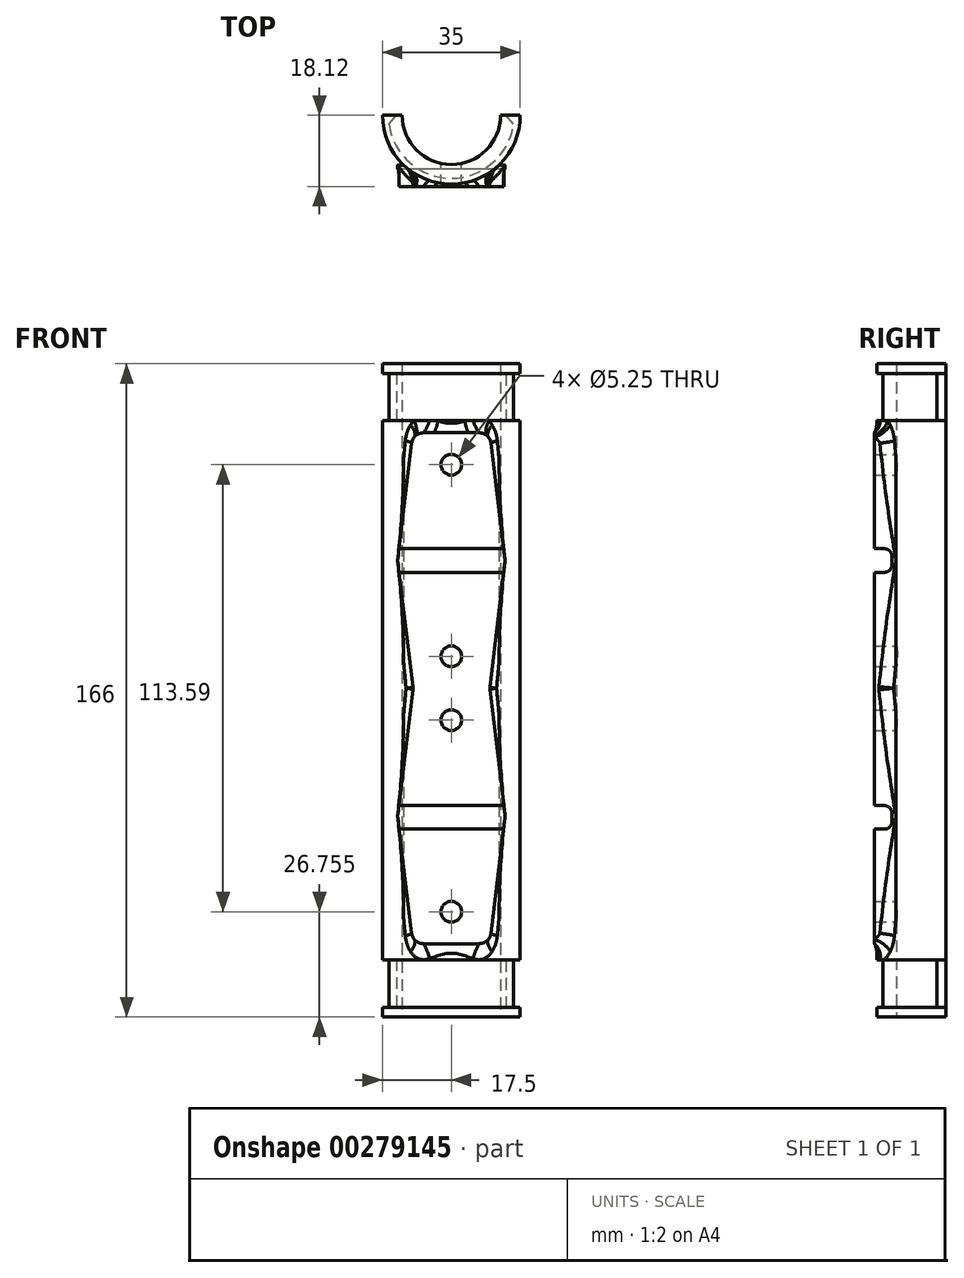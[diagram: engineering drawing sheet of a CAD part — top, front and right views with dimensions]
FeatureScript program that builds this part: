
annotation { "Feature Type Name" : "Feature", "Feature Type Description" : "" }
export const myFeature = defineFeature(function(context is Context, id is Id, definition is map)
    precondition{}
    {
        {
            var Q0;
            Q0=qCreatedBy(makeId("Front.planeOp"),FACE);
            var sketch = newSketch(context, id + "F0", { "sketchPlane" : qUnion([Q0])});
            skLineSegment(sketch, "E0", {"start": v(-13.65, 0) * mm, "end": v(-9.75, 32.45) * mm});
            skLineSegment(sketch, "E1", {"start": v(-9.75, 32.45) * mm, "end": v(9.75, 32.45) * mm});
            skLineSegment(sketch, "E2", {"start": v(9.75, 32.45) * mm, "end": v(13.65, 0) * mm});
            skLineSegment(sketch, "E3.MirrorCS", {"start": v(-13.65, 0) * mm, "end": v(-9.75, -32.45) * mm});
            skLineSegment(sketch, "E4.MirrorCS", {"start": v(9.75, -32.45) * mm, "end": v(13.65, 0) * mm});
            skLineSegment(sketch, "E5.MirrorCS", {"start": v(-9.75, -32.45) * mm, "end": v(9.75, -32.45) * mm});
            skCircle(sketch, "E6", {"center": v(0, 24.35) * mm, "radius": 2.63 * mm});
            skCircle(sketch, "E7.MirrorC", {"center": v(0, -24.35) * mm, "radius": 2.63 * mm});
            skLineSegment(sketch, "E8", {"start": v(-60.1, -32.45) * mm, "end": v(71.13, -32.45) * mm});
            skLineSegment(sketch, "E9.MirrorCS", {"start": v(-13.65, -64.9) * mm, "end": v(-9.75, -32.45) * mm});
            skLineSegment(sketch, "E10.MirrorCS", {"start": v(9.75, -32.45) * mm, "end": v(13.65, -64.9) * mm});
            skLineSegment(sketch, "E11.MirrorCS", {"start": v(9.75, -97.35) * mm, "end": v(13.65, -64.9) * mm});
            skCircle(sketch, "E12.MirrorC", {"center": v(0, -89.25) * mm, "radius": 2.63 * mm});
            skCircle(sketch, "E13.MirrorC", {"center": v(0, -40.56) * mm, "radius": 2.63 * mm});
            skLineSegment(sketch, "E14.MirrorCS", {"start": v(-13.65, -64.9) * mm, "end": v(-9.75, -97.35) * mm});
            skLineSegment(sketch, "E15.MirrorCS", {"start": v(-9.75, -97.35) * mm, "end": v(9.75, -97.35) * mm});
            skSolve(sketch);
        }
        {
            var Q0;
            Q0=makeQuery(id+"F0.imprint","IMPRINT",FACE,{"disambiguationData":[TD([[makeQuery(id+"F0.imprint","IMPRINT",EDGE,{"derivedFrom":sQuery(id+"F0.wireOp",EDGE,"E0")}),-1.0]])]});
            extrude(context, id + "F1", {"entities" : qUnion([Q0]), "depth" : 5.5 * mm});
        }
        {
            var Q0;
            Q0=qCreatedBy(makeId("Top.planeOp"),FACE);
            var sketch = newSketch(context, id + "F2", { "sketchPlane" : qUnion([Q0])});
            skCircle(sketch, "E16", {"center": v(0, 12.62) * mm, "radius": 12.5 * mm});
            skCircle(sketch, "E17", {"center": v(0, 12.62) * mm, "radius": 17.5 * mm});
            skLineSegment(sketch, "E18", {"start": v(-24.24, 12.62) * mm, "end": v(25.02, 12.62) * mm});
            skLineSegment(sketch, "E19", {"start": v(25.02, 12.62) * mm, "end": v(2.17, 34.86) * mm});
            skLineSegment(sketch, "E20", {"start": v(2.17, 34.86) * mm, "end": v(-24.24, 12.62) * mm});
            skSolve(sketch);
        }
        {
            var Q0;
            {var subQ0=sQuery(id+"F2.wireOp",EDGE,"E18");var subQ1=sQuery(id+"F2.wireOp",EDGE,"E16");var subQ2=makeQuery(id+"F2.imprint","INTERSECT",VERTEX,{"disambiguationData":[OD(0.0)],"derivedFrom":[subQ1,subQ0]});Q0=makeQuery(id+"F2.imprint","IMPRINT",FACE,{"disambiguationData":[TD([[makeQuery(id+"F2.imprint","IMPRINT",EDGE,{"disambiguationData":[TD([[subQ2,-1.0]])],"derivedFrom":subQ1}),-1.0]])]});}
            var Q1;
            Q1=makeQuery(id+"F1.opExtrude","SWEPT_FACE",FACE,{"disambiguationData":[OSD([sQuery(id+"F0.wireOp",EDGE,"E1")])]});
            extrude(context, id + "F3", {"entities" : qUnion([Q0]), "operationType" : NewBodyOperationType.ADD, "endBoundEntityFace" : qUnion([Q1]), "depth" : 50 * mm});
        }
        {
            var Q0;
            Q0=qCreatedBy(makeId("Front.planeOp"),FACE);
            var sketch = newSketch(context, id + "F4", { "sketchPlane" : qUnion([Q0])});
            skCircle(sketch, "E21", {"center": v(0, 24.35) * mm, "radius": 2.62 * mm});
            skCircle(sketch, "E22.MirrorC", {"center": v(0, -24.35) * mm, "radius": 2.62 * mm});
            skSolve(sketch);
        }
        {
            var Q0;
            Q0 = qSketchRegion(id + "F4", true);
            extrude(context, id + "F5", {"entities" : qUnion([Q0]), "operationType" : NewBodyOperationType.REMOVE, "endBound" : BoundingType.SYMMETRIC, "oppositeDirection" : true, "depth" : 25 * mm});
        }
        {
            var Q0;
            {var subQ0=sQuery(id+"F2.wireOp",EDGE,"E18");var subQ1=sQuery(id+"F2.wireOp",EDGE,"E16");var subQ2=makeQuery(id+"F2.imprint","INTERSECT",VERTEX,{"disambiguationData":[OD(0.0)],"derivedFrom":[subQ1,subQ0]});Q0=makeQuery(id+"F2.imprint","IMPRINT",FACE,{"disambiguationData":[TD([[makeQuery(id+"F2.imprint","IMPRINT",EDGE,{"disambiguationData":[TD([[subQ2,-1.0]])],"derivedFrom":subQ1}),-1.0]])]});}
            extrude(context, id + "F6", {"entities" : qUnion([Q0]), "operationType" : NewBodyOperationType.ADD, "oppositeDirection" : true, "depth" : 116 * mm});
        }
        {
            var Q0;
            {var subQ1=sQuery(id+"F0.wireOp",EDGE,"E9.MirrorCS");Q0=makeQuery(id+"F0.imprint","IMPRINT",FACE,{"disambiguationData":[TD([[makeQuery(id+"F0.imprint","IMPRINT",EDGE,{"derivedFrom":subQ1}),-1.0]])]});}
            var Q1;
            Q1=makeQuery(id+"F1.opExtrude","CAP_FACE",FACE,{"disambiguationData":[OSD([sQuery(id+"F0.wireOp",EDGE,"E0"),sQuery(id+"F0.wireOp",EDGE,"E1"),sQuery(id+"F0.wireOp",EDGE,"E2"),sQuery(id+"F0.wireOp",EDGE,"E3.MirrorCS"),sQuery(id+"F0.wireOp",EDGE,"E4.MirrorCS"),sQuery(id+"F0.wireOp",EDGE,"E6"),sQuery(id+"F0.wireOp",EDGE,"E7.MirrorC"),sQuery(id+"F0.wireOp",EDGE,"E8")])],"isStart":false});
            extrude(context, id + "F7", {"entities" : qUnion([Q0]), "operationType" : NewBodyOperationType.ADD, "endBound" : BoundingType.UP_TO_SURFACE, "endBoundEntityFace" : qUnion([Q1]), "depth" : 5.25 * mm});
        }
        {
            var Q0;
            Q0=qCreatedBy(makeId("Front.planeOp"),FACE);
            var sketch = newSketch(context, id + "F8", { "sketchPlane" : qUnion([Q0])});
            skCircle(sketch, "E23", {"center": v(0, -24.34) * mm, "radius": 2.62 * mm});
            skSolve(sketch);
        }
        {
            var Q0;
            Q0 = qSketchRegion(id + "F8", true);
            extrude(context, id + "F9", {"entities" : qUnion([Q0]), "operationType" : NewBodyOperationType.REMOVE, "endBound" : BoundingType.SYMMETRIC, "depth" : 42.4 * mm});
        }
        {
            var Q0;
            Q0=qCreatedBy(makeId("Front.planeOp"),FACE);
            var sketch = newSketch(context, id + "F10", { "sketchPlane" : qUnion([Q0])});
            skCircle(sketch, "E24", {"center": v(0, -40.56) * mm, "radius": 2.62 * mm});
            skCircle(sketch, "E25", {"center": v(0, -89.25) * mm, "radius": 2.62 * mm});
            skSolve(sketch);
        }
        {
            var Q0;
            Q0 = qSketchRegion(id + "F10", true);
            extrude(context, id + "F11", {"entities" : qUnion([Q0]), "operationType" : NewBodyOperationType.REMOVE, "endBound" : BoundingType.SYMMETRIC, "oppositeDirection" : true, "depth" : 25 * mm});
        }
        {
            var Q0;
            {var subQ0=sQuery(id+"F2.wireOp",EDGE,"E18");var subQ1=makeQuery(id+"F2.imprint","IMPRINT",EDGE,{"disambiguationData":[TD([[makeQuery(id+"F2.imprint","INTERSECT",VERTEX,{"disambiguationData":[OD(1.0)],"derivedFrom":[sQuery(id+"F2.wireOp",EDGE,"E17"),subQ0]}),-1.0]])],"derivedFrom":subQ0});Q0=makeQuery(id+"F6.boolean.opBoolean","MERGE",FACE,{"derivedFrom":[makeQuery(id+"F3.opExtrude","SWEPT_FACE",FACE,{"disambiguationData":[OSD([subQ0]),TDD([subQ1])]}),makeQuery(id+"F6.opExtrude","SWEPT_FACE",FACE,{"disambiguationData":[OSD([subQ0]),TDD([subQ1])]})]});}
            var sketch = newSketch(context, id + "F12", { "sketchPlane" : qUnion([Q0])});
            skLineSegment(sketch, "E26.bottom", {"start": v(17.5, 47.5) * mm, "end": v(16, 47.5) * mm});
            skLineSegment(sketch, "E26.top", {"start": v(17.5, 35.5) * mm, "end": v(16, 35.5) * mm});
            skLineSegment(sketch, "E26.left", {"start": v(17.5, 47.5) * mm, "end": v(17.5, 35.5) * mm});
            skLineSegment(sketch, "E26.right", {"start": v(16, 47.5) * mm, "end": v(16, 35.5) * mm});
            skLineSegment(sketch, "E27.bottom", {"start": v(17.5, -113.5) * mm, "end": v(16, -113.5) * mm});
            skLineSegment(sketch, "E27.top", {"start": v(17.5, -101.5) * mm, "end": v(16, -101.5) * mm});
            skLineSegment(sketch, "E27.left", {"start": v(17.5, -113.5) * mm, "end": v(17.5, -101.5) * mm});
            skLineSegment(sketch, "E27.right", {"start": v(16, -113.5) * mm, "end": v(16, -101.5) * mm});
            skSolve(sketch);
        }
        {
            var Q0;
            Q0=makeQuery(id+"F12.imprint","IMPRINT",FACE,{"disambiguationData":[TD([[makeQuery(id+"F12.imprint","IMPRINT",EDGE,{"derivedFrom":sQuery(id+"F12.wireOp",EDGE,"E27.bottom")}),-1.0]])]});
            var Q1;
            Q1=makeQuery(id+"F12.imprint","IMPRINT",FACE,{"disambiguationData":[TD([[makeQuery(id+"F12.imprint","IMPRINT",EDGE,{"derivedFrom":sQuery(id+"F12.wireOp",EDGE,"E26.bottom")}),1.0]])]});
            var Q2;
            {var subQ0=sQuery(id+"F2.wireOp",EDGE,"E16");Q2=makeQuery(id+"F6.boolean.opBoolean","MERGE",FACE,{"derivedFrom":[makeQuery(id+"F3.opExtrude","SWEPT_FACE",FACE,{"disambiguationData":[OSD([subQ0])]}),makeQuery(id+"F6.opExtrude","SWEPT_FACE",FACE,{"disambiguationData":[OSD([subQ0])]})]});}
            revolve(context, id + "F13", {"operationType" : NewBodyOperationType.REMOVE, "entities" : qUnion([Q0, Q1]), "axis" : qUnion([Q2]), "revolveType" : RevolveType.FULL, "oppositeDirection" : true});
        }
        {
            var Q0;
            Q0=makeQuery(id+"F1.opExtrude","SWEPT_EDGE",EDGE,{"disambiguationData":[OSD([sQuery(id+"F0.wireOp",EDGE,"E0"),sQuery(id+"F0.wireOp",EDGE,"E1")])]});
            var Q1;
            Q1=makeQuery(id+"F1.opExtrude","SWEPT_EDGE",EDGE,{"disambiguationData":[OSD([sQuery(id+"F0.wireOp",EDGE,"E0"),sQuery(id+"F0.wireOp",EDGE,"E3.MirrorCS")])]});
            var Q2;
            {var subQ0=sQuery(id+"F0.wireOp",EDGE,"E9.MirrorCS");var subQ1=sQuery(id+"F0.wireOp",EDGE,"E8");var subQ2=sQuery(id+"F0.wireOp",EDGE,"E3.MirrorCS");Q2=makeQuery(id+"F7.boolean.opBoolean","MERGE",EDGE,{"derivedFrom":[makeQuery(id+"F1.opExtrude","SWEPT_EDGE",EDGE,{"disambiguationData":[OSD([subQ2,subQ1,subQ0])]}),makeQuery(id+"F7.opExtrude","SWEPT_EDGE",EDGE,{"disambiguationData":[OSD([subQ2,subQ1,subQ0])]})]});}
            var Q3;
            Q3=makeQuery(id+"F7.opExtrude","SWEPT_EDGE",EDGE,{"disambiguationData":[OSD([sQuery(id+"F0.wireOp",EDGE,"E9.MirrorCS"),sQuery(id+"F0.wireOp",EDGE,"E14.MirrorCS")])]});
            var Q4;
            Q4=makeQuery(id+"F7.opExtrude","SWEPT_EDGE",EDGE,{"disambiguationData":[OSD([sQuery(id+"F0.wireOp",EDGE,"E14.MirrorCS"),sQuery(id+"F0.wireOp",EDGE,"E15.MirrorCS")])]});
            var Q5;
            Q5=makeQuery(id+"F7.opExtrude","SWEPT_EDGE",EDGE,{"disambiguationData":[OSD([sQuery(id+"F0.wireOp",EDGE,"E11.MirrorCS"),sQuery(id+"F0.wireOp",EDGE,"E15.MirrorCS")])]});
            var Q6;
            Q6=makeQuery(id+"F7.opExtrude","SWEPT_EDGE",EDGE,{"disambiguationData":[OSD([sQuery(id+"F0.wireOp",EDGE,"E10.MirrorCS"),sQuery(id+"F0.wireOp",EDGE,"E11.MirrorCS")])]});
            var Q7;
            {var subQ0=sQuery(id+"F0.wireOp",EDGE,"E10.MirrorCS");var subQ1=sQuery(id+"F0.wireOp",EDGE,"E8");var subQ2=sQuery(id+"F0.wireOp",EDGE,"E4.MirrorCS");Q7=makeQuery(id+"F7.boolean.opBoolean","MERGE",EDGE,{"derivedFrom":[makeQuery(id+"F1.opExtrude","SWEPT_EDGE",EDGE,{"disambiguationData":[OSD([subQ2,subQ1,subQ0])]}),makeQuery(id+"F7.opExtrude","SWEPT_EDGE",EDGE,{"disambiguationData":[OSD([subQ2,subQ1,subQ0])]})]});}
            var Q8;
            Q8=makeQuery(id+"F1.opExtrude","SWEPT_EDGE",EDGE,{"disambiguationData":[OSD([sQuery(id+"F0.wireOp",EDGE,"E2"),sQuery(id+"F0.wireOp",EDGE,"E4.MirrorCS")])]});
            var Q9;
            Q9=makeQuery(id+"F1.opExtrude","SWEPT_EDGE",EDGE,{"disambiguationData":[OSD([sQuery(id+"F0.wireOp",EDGE,"E1"),sQuery(id+"F0.wireOp",EDGE,"E2")])]});
            fillet(context, id + "F14", {"entities" : qUnion([Q0, Q1, Q2, Q3, Q4, Q5, Q6, Q7, Q8, Q9]), "radius" : 3 * mm, "tangentPropagation" : true, "allowEdgeOverflow" : false});
        }
        {
            var Q0;
            Q0=makeQuery(id+"F6.boolean.opBoolean","INTERSECT",EDGE,{"derivedFrom":[makeQuery(id+"F1.opExtrude","SWEPT_FACE",FACE,{"disambiguationData":[OSD([sQuery(id+"F0.wireOp",EDGE,"E3.MirrorCS")])]}),makeQuery(id+"F6.opExtrude","SWEPT_FACE",FACE,{"disambiguationData":[OSD([sQuery(id+"F2.wireOp",EDGE,"E17")])]})]});
            var Q1;
            Q1=makeQuery(id+"F3.boolean.opBoolean","INTERSECT",EDGE,{"derivedFrom":[makeQuery(id+"F1.opExtrude","SWEPT_FACE",FACE,{"disambiguationData":[OSD([sQuery(id+"F0.wireOp",EDGE,"E0")])]}),makeQuery(id+"F3.opExtrude","SWEPT_FACE",FACE,{"disambiguationData":[OSD([sQuery(id+"F2.wireOp",EDGE,"E17")])]})]});
            var Q2;
            {var subQ0=sQuery(id+"F2.wireOp",EDGE,"E17");var subQ5=sQuery(id+"F0.wireOp",EDGE,"E0");Q2=makeQuery(id+"F7.boolean.opBoolean","INTERSECT",EDGE,{"derivedFrom":[makeQuery(id+"F6.boolean.opBoolean","MERGE",FACE,{"derivedFrom":[makeQuery(id+"F3.boolean.opBoolean","SPLIT",FACE,{"disambiguationData":[TD([makeQuery(id+"F1.opExtrude","SWEPT_FACE",FACE,{"disambiguationData":[OSD([subQ5])]})])],"derivedFrom":makeQuery(id+"F3.opExtrude","SWEPT_FACE",FACE,{"disambiguationData":[OSD([subQ0])]})}),makeQuery(id+"F6.opExtrude","SWEPT_FACE",FACE,{"disambiguationData":[OSD([subQ0])]})]}),makeQuery(id+"F7.opExtrude","SWEPT_FACE",FACE,{"disambiguationData":[OSD([sQuery(id+"F0.wireOp",EDGE,"E14.MirrorCS")])]})]});}
            var Q3;
            {var subQ0=sQuery(id+"F2.wireOp",EDGE,"E17");var subQ5=sQuery(id+"F0.wireOp",EDGE,"E0");Q3=makeQuery(id+"F7.boolean.opBoolean","INTERSECT",EDGE,{"derivedFrom":[makeQuery(id+"F6.boolean.opBoolean","MERGE",FACE,{"derivedFrom":[makeQuery(id+"F3.boolean.opBoolean","SPLIT",FACE,{"disambiguationData":[TD([makeQuery(id+"F1.opExtrude","SWEPT_FACE",FACE,{"disambiguationData":[OSD([subQ5])]})])],"derivedFrom":makeQuery(id+"F3.opExtrude","SWEPT_FACE",FACE,{"disambiguationData":[OSD([subQ0])]})}),makeQuery(id+"F6.opExtrude","SWEPT_FACE",FACE,{"disambiguationData":[OSD([subQ0])]})]}),makeQuery(id+"F7.opExtrude","SWEPT_FACE",FACE,{"disambiguationData":[OSD([sQuery(id+"F0.wireOp",EDGE,"E10.MirrorCS")])]})]});}
            fillet(context, id + "F15", {"entities" : qUnion([Q0, Q1, Q2, Q3]), "radius" : 5 * mm, "tangentPropagation" : true, "allowEdgeOverflow" : false});
        }
        {
            var Q0;
            {var subQ0=sQuery(id+"F0.wireOp",EDGE,"E8");var subQ1=sQuery(id+"F0.wireOp",EDGE,"E7.MirrorC");var subQ2=sQuery(id+"F0.wireOp",EDGE,"E6");var subQ3=sQuery(id+"F0.wireOp",EDGE,"E4.MirrorCS");var subQ4=sQuery(id+"F0.wireOp",EDGE,"E3.MirrorCS");var subQ5=sQuery(id+"F0.wireOp",EDGE,"E2");var subQ6=sQuery(id+"F0.wireOp",EDGE,"E1");var subQ7=sQuery(id+"F0.wireOp",EDGE,"E0");Q0=makeQuery(id+"F7.boolean.opBoolean","MERGE",FACE,{"derivedFrom":[makeQuery(id+"F1.opExtrude","CAP_FACE",FACE,{"disambiguationData":[OSD([subQ7,subQ6,subQ5,subQ4,subQ3,subQ2,subQ1,subQ0])],"isStart":false}),makeQuery(id+"F7.opExtrude","CAP_FACE",FACE,{"disambiguationData":[OSD([subQ7,subQ6,subQ5,subQ4,subQ3,subQ2,subQ1,subQ0])],"isStart":false})]});}
            var sketch = newSketch(context, id + "F16", { "sketchPlane" : qUnion([Q0])});
            skLineSegment(sketch, "E28.bottom", {"start": v(25.56, -3) * mm, "end": v(-25.56, -3) * mm});
            skLineSegment(sketch, "E28.top", {"start": v(25.56, 3) * mm, "end": v(-25.56, 3) * mm});
            skLineSegment(sketch, "E28.left", {"start": v(25.56, -3) * mm, "end": v(25.56, 3) * mm});
            skLineSegment(sketch, "E28.right", {"start": v(-25.56, -3) * mm, "end": v(-25.56, 3) * mm});
            skPoint(sketch, "E28.middle", {"position": v(0, 0) * mm});
            skLineSegment(sketch, "E29", {"start": v(-13.6, -65.26) * mm, "end": v(49, -65.26) * mm});
            skLineSegment(sketch, "E30.bottom", {"start": v(25, -68.26) * mm, "end": v(-25, -68.26) * mm});
            skLineSegment(sketch, "E30.top", {"start": v(25, -62.26) * mm, "end": v(-25, -62.26) * mm});
            skLineSegment(sketch, "E30.left", {"start": v(25, -68.26) * mm, "end": v(25, -62.26) * mm});
            skLineSegment(sketch, "E30.right", {"start": v(-25, -68.26) * mm, "end": v(-25, -62.26) * mm});
            skPoint(sketch, "E30.middle", {"position": v(0, -65.26) * mm});
            skSolve(sketch);
        }
        {
            var Q0;
            Q0 = qSketchRegion(id + "F16", true);
            extrude(context, id + "F17", {"entities" : qUnion([Q0]), "operationType" : NewBodyOperationType.REMOVE, "oppositeDirection" : true, "depth" : 4.5 * mm});
        }
        {
            var Q0;
            Q0=makeQuery(id+"F17.boolean.opBoolean","COPY",EDGE,{"derivedFrom":makeQuery(id+"F17.opExtrude","CAP_EDGE",EDGE,{"disambiguationData":[OSD([sQuery(id+"F16.wireOp",EDGE,"E30.bottom")])],"isStart":false})});
            var Q1;
            Q1=makeQuery(id+"F17.boolean.opBoolean","COPY",EDGE,{"derivedFrom":makeQuery(id+"F17.opExtrude","CAP_EDGE",EDGE,{"disambiguationData":[OSD([sQuery(id+"F16.wireOp",EDGE,"E30.top")])],"isStart":false})});
            var Q2;
            Q2=makeQuery(id+"F17.boolean.opBoolean","COPY",EDGE,{"derivedFrom":makeQuery(id+"F17.opExtrude","CAP_EDGE",EDGE,{"disambiguationData":[OSD([sQuery(id+"F16.wireOp",EDGE,"E28.top")])],"isStart":false})});
            var Q3;
            Q3=makeQuery(id+"F17.boolean.opBoolean","COPY",EDGE,{"derivedFrom":makeQuery(id+"F17.opExtrude","CAP_EDGE",EDGE,{"disambiguationData":[OSD([sQuery(id+"F16.wireOp",EDGE,"E28.bottom")])],"isStart":false})});
            fillet(context, id + "F18", {"entities" : qUnion([Q0, Q1, Q2, Q3]), "radius" : 2 * mm, "tangentPropagation" : true, "allowEdgeOverflow" : false});
        }
        {
            var Q0;
            {var subQ0=sQuery(id+"F2.wireOp",EDGE,"E18");var subQ1=makeQuery(id+"F2.imprint","IMPRINT",EDGE,{"disambiguationData":[TD([[makeQuery(id+"F2.imprint","INTERSECT",VERTEX,{"disambiguationData":[OD(1.0)],"derivedFrom":[sQuery(id+"F2.wireOp",EDGE,"E17"),subQ0]}),-1.0]])],"derivedFrom":subQ0});Q0=makeQuery(id+"F13.boolean.opBoolean","INTERSECT",EDGE,{"derivedFrom":[makeQuery(id+"F6.boolean.opBoolean","MERGE",FACE,{"derivedFrom":[makeQuery(id+"F3.opExtrude","SWEPT_FACE",FACE,{"disambiguationData":[OSD([subQ0]),TDD([subQ1])]}),makeQuery(id+"F6.opExtrude","SWEPT_FACE",FACE,{"disambiguationData":[OSD([subQ0]),TDD([subQ1])]})]}),makeQuery(id+"F13.opRevolve","SWEPT_FACE",FACE,{"disambiguationData":[OSD([sQuery(id+"F12.wireOp",EDGE,"E26.right")])]})]});}
            var Q1;
            {var subQ0=sQuery(id+"F2.wireOp",EDGE,"E18");var subQ1=makeQuery(id+"F2.imprint","IMPRINT",EDGE,{"disambiguationData":[TD([[makeQuery(id+"F2.imprint","INTERSECT",VERTEX,{"disambiguationData":[OD(1.0)],"derivedFrom":[sQuery(id+"F2.wireOp",EDGE,"E17"),subQ0]}),-1.0]])],"derivedFrom":subQ0});Q1=makeQuery(id+"F13.boolean.opBoolean","INTERSECT",EDGE,{"derivedFrom":[makeQuery(id+"F6.boolean.opBoolean","MERGE",FACE,{"derivedFrom":[makeQuery(id+"F3.opExtrude","SWEPT_FACE",FACE,{"disambiguationData":[OSD([subQ0]),TDD([subQ1])]}),makeQuery(id+"F6.opExtrude","SWEPT_FACE",FACE,{"disambiguationData":[OSD([subQ0]),TDD([subQ1])]})]}),makeQuery(id+"F13.opRevolve","SWEPT_FACE",FACE,{"disambiguationData":[OSD([sQuery(id+"F12.wireOp",EDGE,"E27.right")])]})]});}
            var Q2;
            {var subQ0=sQuery(id+"F2.wireOp",EDGE,"E18");var subQ1=makeQuery(id+"F2.imprint","IMPRINT",EDGE,{"disambiguationData":[TD([[makeQuery(id+"F2.imprint","INTERSECT",VERTEX,{"disambiguationData":[OD(0.0)],"derivedFrom":[sQuery(id+"F2.wireOp",EDGE,"E17"),subQ0]}),1.0]])],"derivedFrom":subQ0});Q2=makeQuery(id+"F13.boolean.opBoolean","INTERSECT",EDGE,{"derivedFrom":[makeQuery(id+"F6.boolean.opBoolean","MERGE",FACE,{"derivedFrom":[makeQuery(id+"F3.opExtrude","SWEPT_FACE",FACE,{"disambiguationData":[OSD([subQ0]),TDD([subQ1])]}),makeQuery(id+"F6.opExtrude","SWEPT_FACE",FACE,{"disambiguationData":[OSD([subQ0]),TDD([subQ1])]})]}),makeQuery(id+"F13.opRevolve","SWEPT_FACE",FACE,{"disambiguationData":[OSD([sQuery(id+"F12.wireOp",EDGE,"E27.right")])]})]});}
            var Q3;
            {var subQ0=sQuery(id+"F2.wireOp",EDGE,"E18");var subQ1=makeQuery(id+"F2.imprint","IMPRINT",EDGE,{"disambiguationData":[TD([[makeQuery(id+"F2.imprint","INTERSECT",VERTEX,{"disambiguationData":[OD(0.0)],"derivedFrom":[sQuery(id+"F2.wireOp",EDGE,"E17"),subQ0]}),1.0]])],"derivedFrom":subQ0});Q3=makeQuery(id+"F13.boolean.opBoolean","INTERSECT",EDGE,{"derivedFrom":[makeQuery(id+"F6.boolean.opBoolean","MERGE",FACE,{"derivedFrom":[makeQuery(id+"F3.opExtrude","SWEPT_FACE",FACE,{"disambiguationData":[OSD([subQ0]),TDD([subQ1])]}),makeQuery(id+"F6.opExtrude","SWEPT_FACE",FACE,{"disambiguationData":[OSD([subQ0]),TDD([subQ1])]})]}),makeQuery(id+"F13.opRevolve","SWEPT_FACE",FACE,{"disambiguationData":[OSD([sQuery(id+"F12.wireOp",EDGE,"E26.right")])]})]});}
            chamfer(context, id + "F19", {"entities" : qUnion([Q0, Q1, Q2, Q3]), "width" : 2 * mm, "tangentPropagation" : true});
        }
    });
